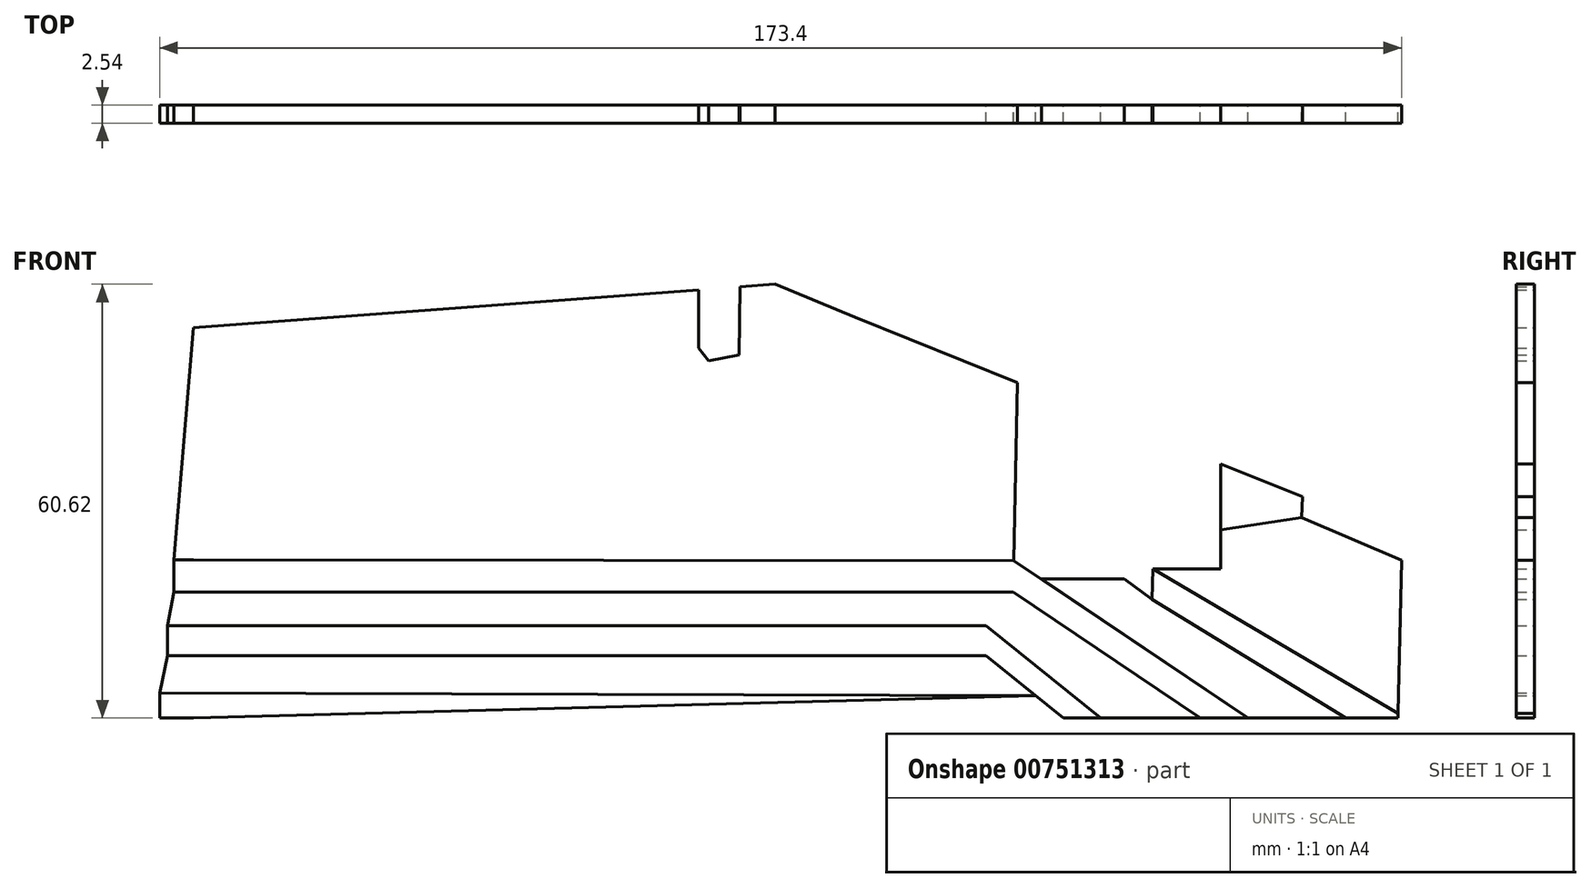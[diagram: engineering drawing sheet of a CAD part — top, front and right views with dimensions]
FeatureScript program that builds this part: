
annotation { "Feature Type Name" : "Feature", "Feature Type Description" : "" }
export const myFeature = defineFeature(function(context is Context, id is Id, definition is map)
    precondition{}
    {
        {
            var Q0;
            Q0=qCreatedBy(makeId("Front.planeOp"),FACE);
            var sketch = newSketch(context, id + "F0", { "sketchPlane" : qUnion([Q0])});
            skSolve(sketch);
        }
        {
            var Q0;
            Q0=qCreatedBy(makeId("Front.planeOp"),FACE);
            var sketch = newSketch(context, id + "F1", { "sketchPlane" : qUnion([Q0])});
            skPoint(sketch, "E0.0", {"position": v(-106, 78.32) * mm});
            skPoint(sketch, "E1.0", {"position": v(-106, -78.96) * mm});
            skPoint(sketch, "E2.0", {"position": v(103.7, -78.96) * mm});
            skPoint(sketch, "E3.0", {"position": v(103.7, 78.32) * mm});
            skLineSegment(sketch, "E4", {"start": v(-106, 78.32) * mm, "end": v(103.7, 78.32) * mm});
            skLineSegment(sketch, "E5", {"start": v(103.7, 78.32) * mm, "end": v(103.7, -78.96) * mm});
            skLineSegment(sketch, "E6", {"start": v(103.7, -78.96) * mm, "end": v(-106, -78.96) * mm});
            skLineSegment(sketch, "E7", {"start": v(-106, -78.96) * mm, "end": v(-106, 78.32) * mm});
            skLineSegment(sketch, "E8", {"start": v(41.54, -59.56) * mm, "end": v(70.36, -78.96) * mm});
            skLineSegment(sketch, "E9", {"start": v(41.54, -59.56) * mm, "end": v(53.09, -59.56) * mm});
            skLineSegment(sketch, "E10", {"start": v(53.09, -59.56) * mm, "end": v(57, -62.42) * mm});
            skLineSegment(sketch, "E11", {"start": v(66.58, -58.13) * mm, "end": v(66.66, 25.24) * mm});
            skLineSegment(sketch, "E12", {"start": v(41.54, -59.56) * mm, "end": v(43.63, 47.23) * mm});
            skLineSegment(sketch, "E13", {"start": v(43.63, 47.23) * mm, "end": v(55.4, 47) * mm});
            skLineSegment(sketch, "E14", {"start": v(55.4, 47) * mm, "end": v(53.09, -59.56) * mm});
            skLineSegment(sketch, "E15", {"start": v(55.4, 47) * mm, "end": v(101.45, 59.45) * mm});
            skLineSegment(sketch, "E16", {"start": v(101.45, 59.45) * mm, "end": v(103.7, 59.45) * mm});
            skLineSegment(sketch, "E17", {"start": v(101.45, 59.45) * mm, "end": v(97.9, -78.96) * mm});
            skLineSegment(sketch, "E18", {"start": v(93.65, 27.22) * mm, "end": v(91.35, -78.96) * mm});
            skLineSegment(sketch, "E19", {"start": v(57, -62.42) * mm, "end": v(59.48, 24.66) * mm});
            skLineSegment(sketch, "E20", {"start": v(59.48, 24.66) * mm, "end": v(93.65, 27.22) * mm});
            skLineSegment(sketch, "E21", {"start": v(57.13, -58.13) * mm, "end": v(66.58, -58.13) * mm});
            skLineSegment(sketch, "E22", {"start": v(57, -62.42) * mm, "end": v(84, -78.96) * mm});
            skLineSegment(sketch, "E23", {"start": v(57.13, -58.13) * mm, "end": v(92.47, -78.96) * mm});
            skLineSegment(sketch, "E24", {"start": v(49.82, -78.96) * mm, "end": v(33.8, -66.1) * mm});
            skLineSegment(sketch, "E25", {"start": v(41.54, -64.05) * mm, "end": v(63.7, -78.96) * mm});
            skLineSegment(sketch, "E26", {"start": v(33.8, -66.1) * mm, "end": v(33.8, -70.28) * mm});
            skLineSegment(sketch, "E27", {"start": v(33.8, -70.28) * mm, "end": v(44.6, -78.96) * mm});
            skLineSegment(sketch, "E28", {"start": v(41.54, -64.05) * mm, "end": v(37.6, -61.4) * mm});
            skLineSegment(sketch, "E29", {"start": v(37.6, -61.4) * mm, "end": v(39.27, 23.95) * mm});
            skLineSegment(sketch, "E30", {"start": v(39.27, 23.95) * mm, "end": v(-4.96, 19.51) * mm});
            skLineSegment(sketch, "E31", {"start": v(-4.96, 19.51) * mm, "end": v(-4.96, -29.02) * mm});
            skLineSegment(sketch, "E32", {"start": v(-0.67, -28.2) * mm, "end": v(0, 20.01) * mm});
            skLineSegment(sketch, "E33", {"start": v(-6.34, 32.45) * mm, "end": v(-6.34, -27.3) * mm});
            skLineSegment(sketch, "E34", {"start": v(-6.34, 32.45) * mm, "end": v(43.63, 47.23) * mm});
            skLineSegment(sketch, "E35", {"start": v(41.54, -59.56) * mm, "end": v(37.68, -56.96) * mm});
            skLineSegment(sketch, "E36", {"start": v(33.8, -66.1) * mm, "end": v(37.6, -61.4) * mm});
            skLineSegment(sketch, "E37", {"start": v(37.68, -56.96) * mm, "end": v(-76.85, -56.86) * mm});
            skPoint(sketch, "E38.orphan", {"position": v(-76.85, -66.1) * mm});
            skLineSegment(sketch, "E39", {"start": v(33.8, -66.1) * mm, "end": v(-76.85, -66.1) * mm});
            skLineSegment(sketch, "E40", {"start": v(33.8, -70.28) * mm, "end": v(-80.5, -70.28) * mm});
            skLineSegment(sketch, "E41", {"start": v(37.6, -61.4) * mm, "end": v(-79.6, -61.4) * mm});
            skLineSegment(sketch, "E42", {"start": v(-76.85, -78.96) * mm, "end": v(40.73, -75.84) * mm});
            skLineSegment(sketch, "E43", {"start": v(40.73, -75.84) * mm, "end": v(-76.85, -75.49) * mm});
            skLineSegment(sketch, "E44", {"start": v(-76.85, -24.4) * mm, "end": v(-79.6, -56.86) * mm});
            skLineSegment(sketch, "E45", {"start": v(-79.6, -56.86) * mm, "end": v(-79.6, -61.4) * mm});
            skLineSegment(sketch, "E46", {"start": v(-76.85, -66.1) * mm, "end": v(-80.5, -66.1) * mm});
            skLineSegment(sketch, "E47", {"start": v(-79.6, -61.4) * mm, "end": v(-80.5, -66.1) * mm});
            skLineSegment(sketch, "E48", {"start": v(-80.5, -66.1) * mm, "end": v(-80.5, -70.28) * mm});
            skLineSegment(sketch, "E49", {"start": v(-76.85, -75.49) * mm, "end": v(-81.58, -75.48) * mm});
            skLineSegment(sketch, "E50", {"start": v(-80.5, -70.28) * mm, "end": v(-81.58, -75.48) * mm});
            skLineSegment(sketch, "E51", {"start": v(-81.58, -75.48) * mm, "end": v(-81.58, -78.96) * mm});
            skLineSegment(sketch, "E52", {"start": v(-76.85, -56.86) * mm, "end": v(-79.6, -56.86) * mm});
            skLineSegment(sketch, "E53", {"start": v(-4.96, -29.02) * mm, "end": v(-6.34, -27.3) * mm});
            skLineSegment(sketch, "E54", {"start": v(-4.96, -29.02) * mm, "end": v(-0.67, -28.2) * mm});
            skLineSegment(sketch, "E55", {"start": v(-76.85, -24.4) * mm, "end": v(-6.34, -19.14) * mm});
            skLineSegment(sketch, "E56", {"start": v(38.22, -29.73) * mm, "end": v(15.58, -20.55) * mm});
            skLineSegment(sketch, "E57", {"start": v(66.6, -41.07) * mm, "end": v(78.05, -45.65) * mm});
            skLineSegment(sketch, "E58", {"start": v(78.05, -45.65) * mm, "end": v(79.72, 13.28) * mm});
            skLineSegment(sketch, "E59", {"start": v(79.72, 13.28) * mm, "end": v(66.65, 13.54) * mm});
            skLineSegment(sketch, "E60", {"start": v(27.55, 13.54) * mm, "end": v(27.02, -25.18) * mm});
            skLineSegment(sketch, "E61", {"start": v(78.05, -45.65) * mm, "end": v(77.9, -50.95) * mm});
            skLineSegment(sketch, "E62", {"start": v(77.9, -50.95) * mm, "end": v(91.82, -56.95) * mm});
            skLineSegment(sketch, "E63", {"start": v(86.97, -54.86) * mm, "end": v(89.22, 15.14) * mm});
            skLineSegment(sketch, "E64", {"start": v(89.22, 15.14) * mm, "end": v(93.38, 15) * mm});
            skLineSegment(sketch, "E65.trimOffspring", {"start": v(39.06, 13.54) * mm, "end": v(27.55, 13.54) * mm});
            skLineSegment(sketch, "E66.trimOffspring", {"start": v(-0.54, -18.7) * mm, "end": v(4.35, -18.34) * mm});
            skLineSegment(sketch, "E67", {"start": v(38.17, -32.1) * mm, "end": v(15.55, -22.92) * mm});
            skPoint(sketch, "E67.endSnap0", {"position": v(4.35, -18.34) * mm});
            skLineSegment(sketch, "E68", {"start": v(15.55, -22.92) * mm, "end": v(16.22, 19.26) * mm});
            skLineSegment(sketch, "E69", {"start": v(0, 20.01) * mm, "end": v(23.72, 19.07) * mm});
            skLineSegment(sketch, "E70", {"start": v(23.72, 19.07) * mm, "end": v(23.72, 22.39) * mm});
            skLineSegment(sketch, "E71", {"start": v(16.22, 19.26) * mm, "end": v(16.22, 19.37) * mm});
            skLineSegment(sketch, "E72.trimOffspring", {"start": v(66.59, -52.64) * mm, "end": v(77.9, -50.95) * mm});
            skPoint(sketch, "E73.orphan", {"position": v(4.35, -18.38) * mm});
            skLineSegment(sketch, "E74", {"start": v(4.35, -18.34) * mm, "end": v(15.55, -22.92) * mm});
            skLineSegment(sketch, "E75.trimOffspring", {"start": v(66.6, -43.46) * mm, "end": v(77.98, -48.01) * mm});
            skSolve(sketch);
        }
        {
            var Q0;
            {var subQ0=sQuery(id+"F1.wireOp",EDGE,"E42");Q0=makeQuery(id+"F1.imprint","IMPRINT",FACE,{"disambiguationData":[TD([[makeQuery(id+"F1.imprint","IMPRINT",EDGE,{"derivedFrom":subQ0}),1.0]])]});}
            var Q1;
            Q1=makeQuery(id+"F1.imprint","IMPRINT",FACE,{"disambiguationData":[TD([[makeQuery(id+"F1.imprint","IMPRINT",EDGE,{"derivedFrom":sQuery(id+"F1.wireOp",EDGE,"E26")}),-1.0]])]});
            var Q2;
            {var subQ1=sQuery(id+"F1.wireOp",EDGE,"E37");Q2=makeQuery(id+"F1.imprint","IMPRINT",FACE,{"disambiguationData":[TD([[makeQuery(id+"F1.imprint","IMPRINT",EDGE,{"derivedFrom":subQ1}),1.0]])]});}
            var Q3;
            {var subQ2=sQuery(id+"F1.wireOp",EDGE,"E8");Q3=makeQuery(id+"F1.imprint","IMPRINT",FACE,{"disambiguationData":[TD([[makeQuery(id+"F1.imprint","IMPRINT",EDGE,{"derivedFrom":subQ2}),-1.0]])]});}
            var Q4;
            {var subQ3=sQuery(id+"F1.wireOp",EDGE,"E24");Q4=makeQuery(id+"F1.imprint","IMPRINT",FACE,{"disambiguationData":[TD([[makeQuery(id+"F1.imprint","IMPRINT",EDGE,{"derivedFrom":subQ3}),1.0]])]});}
            var Q5;
            {var subQ0=sQuery(id+"F1.wireOp",EDGE,"E22");Q5=makeQuery(id+"F1.imprint","IMPRINT",FACE,{"disambiguationData":[TD([[makeQuery(id+"F1.imprint","IMPRINT",EDGE,{"derivedFrom":subQ0}),1.0]])]});}
            extrude(context, id + "F2", {"entities" : qUnion([Q0, Q1, Q2, Q3, Q4, Q5]), "depth" : 2.54 * mm, "offsetDistance" : 25.4 * mm});
        }
        {
            var Q0;
            {var subQ1=sQuery(id+"F1.wireOp",EDGE,"E40");Q0=makeQuery(id+"F1.imprint","IMPRINT",FACE,{"disambiguationData":[TD([[makeQuery(id+"F1.imprint","IMPRINT",EDGE,{"derivedFrom":subQ1}),1.0]])]});}
            var Q1;
            Q1=makeQuery(id+"F1.imprint","IMPRINT",FACE,{"disambiguationData":[TD([[makeQuery(id+"F1.imprint","IMPRINT",EDGE,{"derivedFrom":sQuery(id+"F1.wireOp",EDGE,"E36")}),1.0]])]});
            var Q2;
            {var subQ1=sQuery(id+"F1.wireOp",EDGE,"E37");Q2=makeQuery(id+"F1.imprint","IMPRINT",FACE,{"disambiguationData":[TD([[makeQuery(id+"F1.imprint","IMPRINT",EDGE,{"derivedFrom":subQ1}),-1.0]])]});}
            var Q3;
            {var subQ1=sQuery(id+"F1.wireOp",EDGE,"E24");Q3=makeQuery(id+"F1.imprint","IMPRINT",FACE,{"disambiguationData":[TD([[makeQuery(id+"F1.imprint","IMPRINT",EDGE,{"derivedFrom":subQ1}),-1.0]])]});}
            var Q4;
            {var subQ1=sQuery(id+"F1.wireOp",EDGE,"E8");Q4=makeQuery(id+"F1.imprint","IMPRINT",FACE,{"disambiguationData":[TD([[makeQuery(id+"F1.imprint","IMPRINT",EDGE,{"derivedFrom":subQ1}),1.0]])]});}
            var Q5;
            {var subQ0=sQuery(id+"F1.wireOp",EDGE,"E72.trimOffspring");Q5=makeQuery(id+"F1.imprint","IMPRINT",FACE,{"disambiguationData":[TD([[makeQuery(id+"F1.imprint","IMPRINT",EDGE,{"derivedFrom":subQ0}),1.0]])]});}
            extrude(context, id + "F3", {"entities" : qUnion([Q0, Q1, Q2, Q3, Q4, Q5]), "depth" : 2.54 * mm, "offsetDistance" : 25.4 * mm});
        }
        {
            var Q0;
            {var subQ1=sQuery(id+"F1.wireOp",EDGE,"E21");Q0=makeQuery(id+"F1.imprint","IMPRINT",FACE,{"disambiguationData":[TD([[makeQuery(id+"F1.imprint","IMPRINT",EDGE,{"derivedFrom":subQ1}),-1.0]])]});}
            extrude(context, id + "F4", {"entities" : qUnion([Q0]), "depth" : 2.54 * mm, "offsetDistance" : 25.4 * mm});
        }
    });
